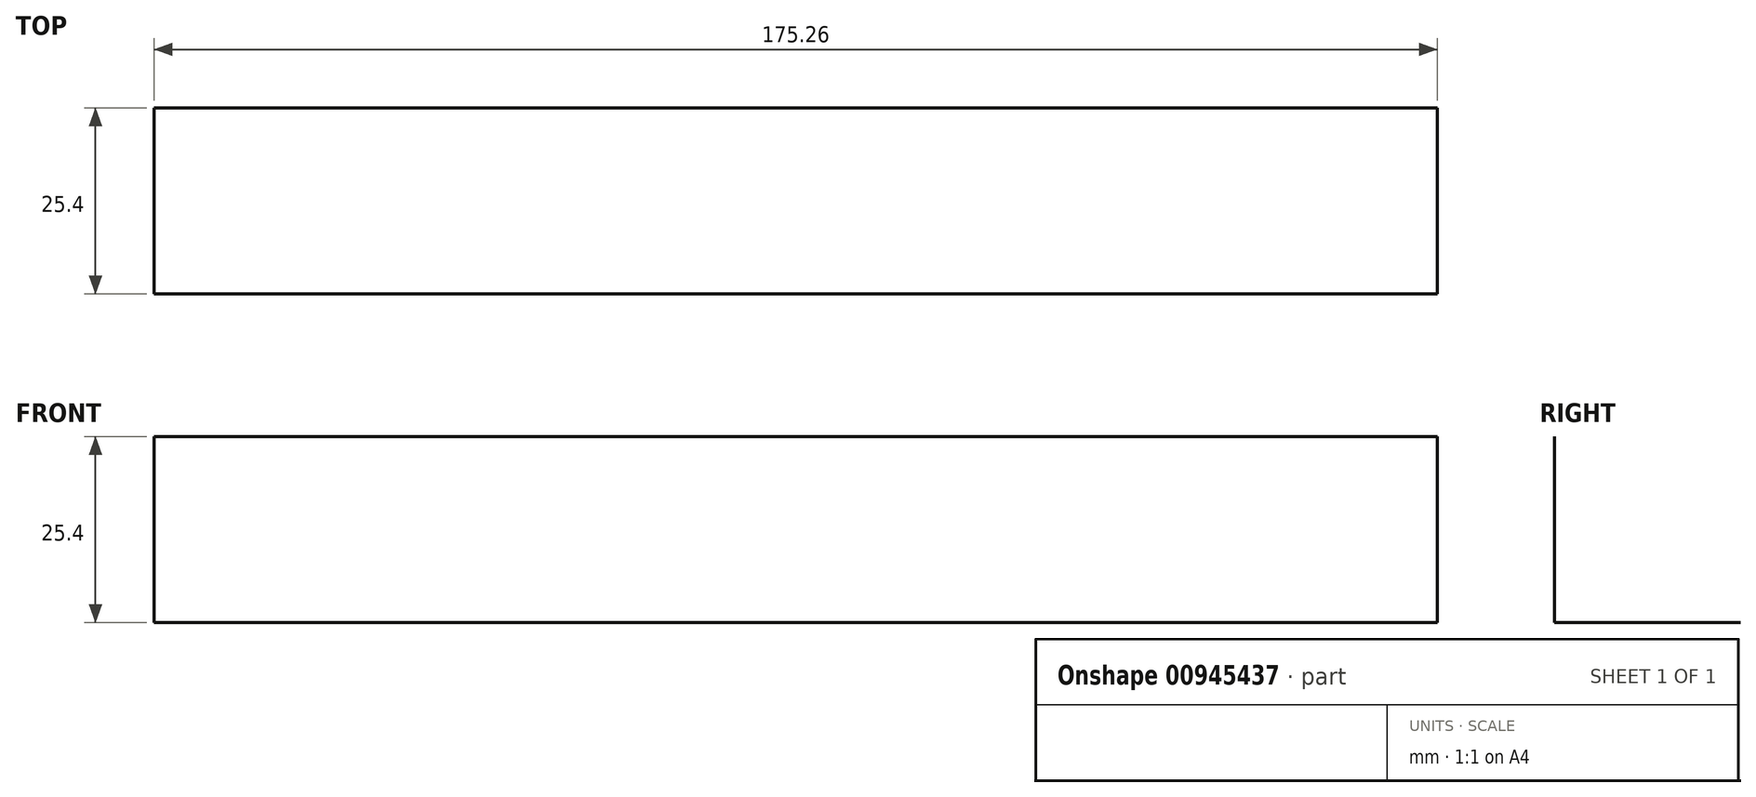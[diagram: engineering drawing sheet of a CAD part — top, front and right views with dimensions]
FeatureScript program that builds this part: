
annotation { "Feature Type Name" : "Feature", "Feature Type Description" : "" }
export const myFeature = defineFeature(function(context is Context, id is Id, definition is map)
    precondition{}
    {
        {
            var Q0;
            Q0=qCreatedBy(makeId("Right.planeOp"),FACE);
            var sketch = newSketch(context, id + "F0", { "sketchPlane" : qUnion([Q0])});
            skLineSegment(sketch, "E0.top", {"start": v(-7.92, -12.42) * mm, "end": v(17.48, -12.42) * mm});
            skLineSegment(sketch, "E0.left", {"start": v(-7.92, 12.98) * mm, "end": v(-7.92, -12.42) * mm});
            skSolve(sketch);
        }
        {
            var Q0;
            Q0=sQuery(id+"F0.wireOp",EDGE,"E0.left");
            var Q1;
            Q1=sQuery(id+"F0.wireOp",EDGE,"E0.top");
            extrude(context, id + "F1", {"bodyType" : ToolBodyType.SURFACE, "surfaceEntities" : qUnion([Q0, Q1]), "depth" : 175.26 * mm, "offsetDistance" : 25.4 * mm});
        }
    });
